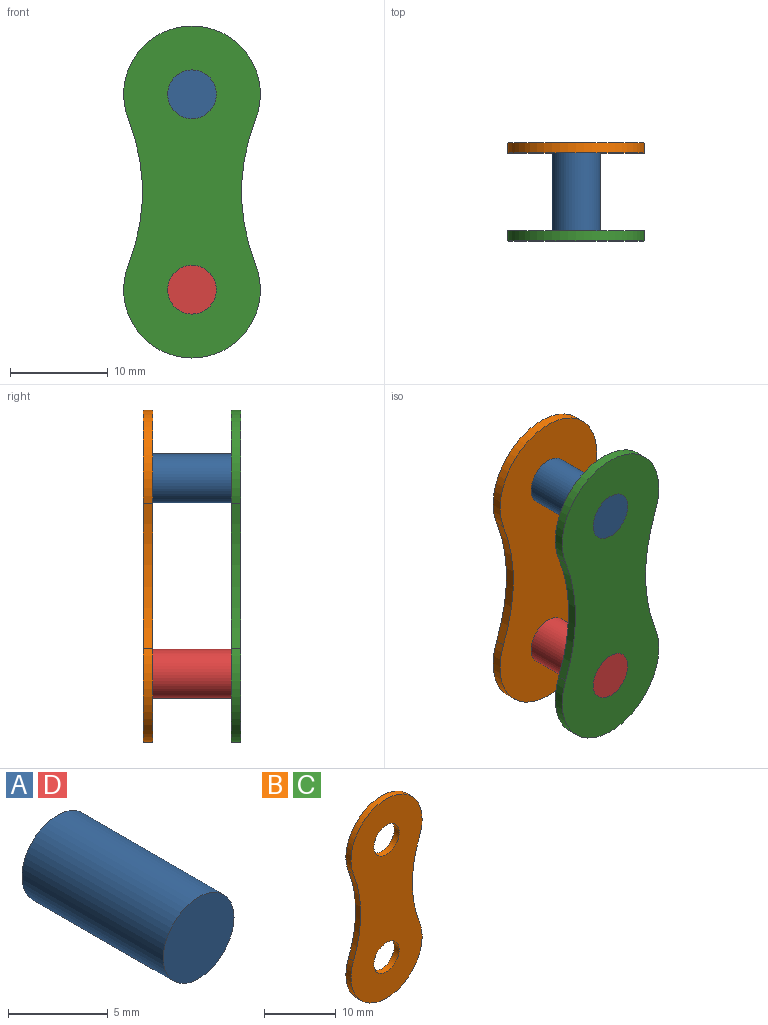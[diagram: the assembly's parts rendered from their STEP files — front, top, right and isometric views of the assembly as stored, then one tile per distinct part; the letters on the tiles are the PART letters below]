
ASSEMBLY  parts=4 mates=3
PART A: 3 faces, bbox 5x10x5 mm
  f0: cylinder r=2.5mm len=10mm, axis (0,1,0), area 157.1mm2, adj f1,f2
  f1: plane 5x5mm, normal (0,-1,0), area 19.6mm2, adj f0
  f2: plane 5x5mm, normal (0,1,0), area 19.6mm2, adj f0
PART B: 8 faces, bbox 14x1x34 mm
  f0: cylinder r=20mm len=14.82mm, axis (0,1,0), area 15.2mm2, adj f1,f5,f6,f7
  f1: cylinder r=7mm len=14mm, axis (0,1,0), area 27.3mm2, adj f0,f2,f6,f7
  f2: cylinder r=20mm len=14.82mm, axis (0,1,0), area 15.2mm2, adj f1,f5,f6,f7
  f3: cylinder r=2.5mm len=5mm, axis (0,1,0), area 15.7mm2, adj f6,f7
  f4: cylinder r=2.5mm len=5mm, axis (0,1,0), area 15.7mm2, adj f6,f7
  f5: cylinder r=7mm len=14mm, axis (0,1,0), area 27.3mm2, adj f0,f2,f6,f7
  f6: plane 34x14mm, normal (0,-1,0), area 349.9mm2, adj f0,f1,f2,f3,f4,f5
  f7: plane 34x14mm, normal (0,1,0), area 349.9mm2, adj f0,f1,f2,f3,f4,f5
PART C: same geometry as B
PART D: same geometry as A
PLACE A t=(27.22,-10.37,-30.48)mm
PLACE B t=(44.78,-10.37,-40.68)mm
PLACE C t=(44.78,-19.37,-40.68)mm
PLACE D t=(27.22,-10.37,-50.48)mm
MATE fastened A.f0 <-> B.f3  axis (0,1,0) through (-0.82,-10.37,27.53)mm
MATE fastened A.f0 <-> C.f3  axis (0,-1,0) through (-0.82,-20.37,27.53)mm
MATE fastened D.f0 <-> C.f1  axis (0,-1,0) through (-0.82,-20.37,7.53)mm
